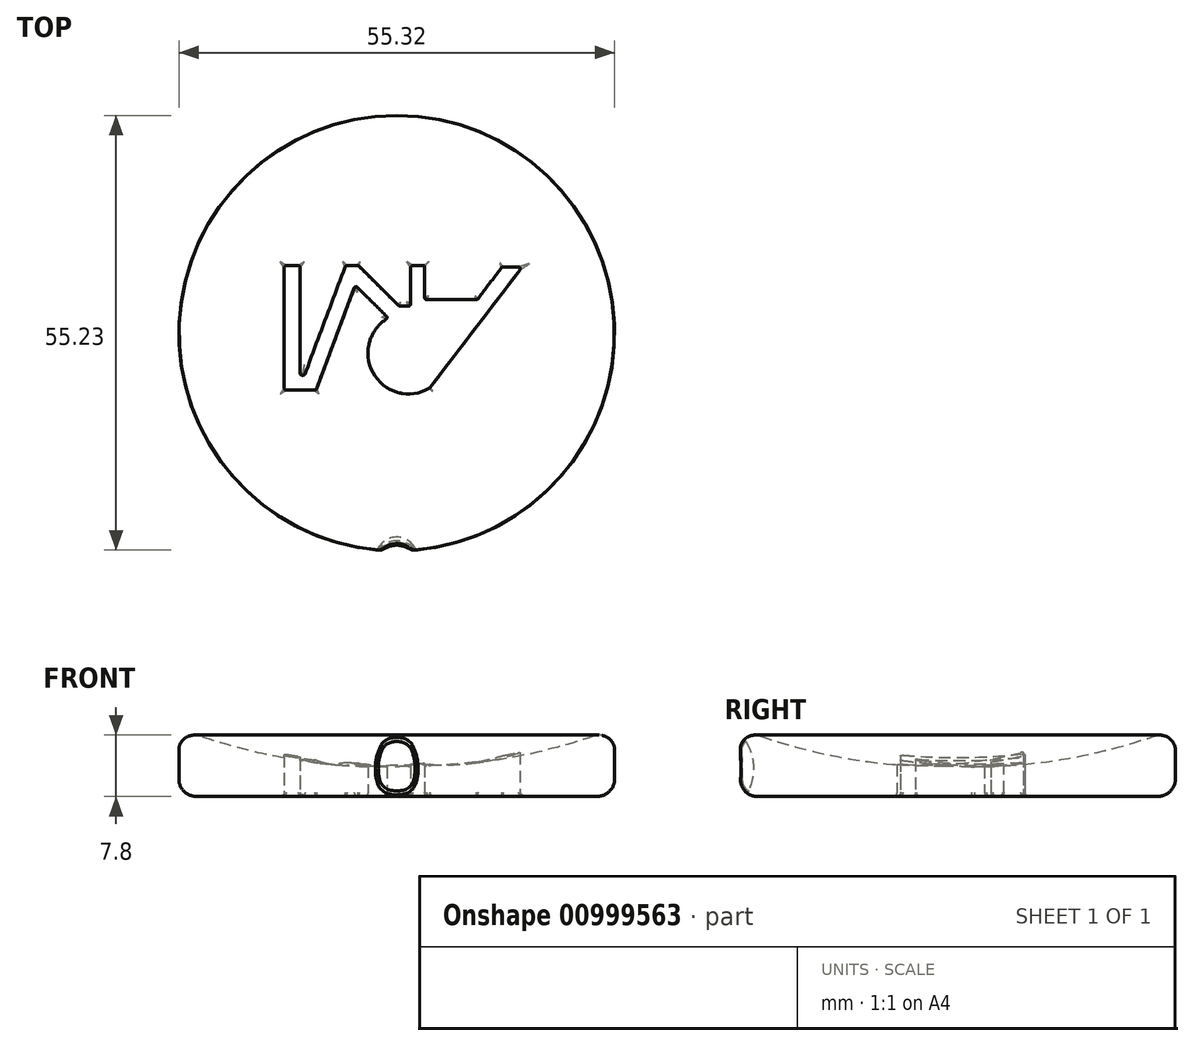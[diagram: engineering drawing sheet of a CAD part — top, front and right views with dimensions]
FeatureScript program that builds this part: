
annotation { "Feature Type Name" : "Feature", "Feature Type Description" : "" }
export const myFeature = defineFeature(function(context is Context, id is Id, definition is map)
    precondition{}
    {
        {
            var Q0;
            Q0=qCreatedBy(makeId("Front.planeOp"),FACE);
            var sketch = newSketch(context, id + "F0", { "sketchPlane" : qUnion([Q0])});
            skLineSegment(sketch, "E0", {"start": v(0, 0) * mm, "end": v(-25.4, 0) * mm});
            skLineSegment(sketch, "E1", {"start": v(0, 0) * mm, "end": v(0, 3.81) * mm});
            skLineSegment(sketch, "E2", {"start": v(-25.16, 7.73) * mm, "end": v(-27.66, 6.26) * mm});
            skLineSegment(sketch, "E3", {"start": v(-25.4, 0) * mm, "end": v(-27.66, 1.82) * mm});
            skLineSegment(sketch, "E4", {"start": v(-27.66, 6.26) * mm, "end": v(-27.66, 1.82) * mm});
            skArc(sketch, "E5", {"start": v(-25.16, 7.73) * mm, "mid": v(-26.72, 7.53) * mm, "end": v(-27.66, 6.26) * mm});
            skArc(sketch, "E6", {"start": v(-25.4, 0) * mm, "mid": v(-26.85, 0.51) * mm, "end": v(-27.66, 1.82) * mm});
            skArc(sketch, "E7", {"start": v(-25.16, 7.73) * mm, "mid": v(-12.76, 4.64) * mm, "end": v(0, 3.81) * mm});
            skSolve(sketch);
        }
        {
            var Q0;
            Q0=qSketchRegion(id+"F0",true);
            var Q1;
            Q1=sQuery(id+"F0.wireOp",EDGE,"E1");
            revolve(context, id + "F1", {"surfaceOperationType" : NewSurfaceOperationType.NEW, "entities" : qUnion([Q0]), "axis" : qUnion([Q1]), "revolveType" : RevolveType.FULL});
        }
        {
            var Q0;
            Q0=makeQuery(id+"F1.opRevolve","SWEPT_FACE",FACE,{"disambiguationData":[OSD([sQuery(id+"F0.wireOp",EDGE,"E0")])]});
            var sketch = newSketch(context, id + "F2", { "sketchPlane" : qUnion([Q0])});
            skLineSegment(sketch, "E8", {"start": v(15.95, -8.4) * mm, "end": v(13.39, -8.4) * mm});
            skLineSegment(sketch, "E9", {"start": v(13.39, -8.4) * mm, "end": v(10.22, -4.26) * mm});
            skLineSegment(sketch, "E10", {"start": v(-5.26, -6.09) * mm, "end": v(-1.09, -1.93) * mm});
            skLineSegment(sketch, "E11", {"start": v(1.78, -8.57) * mm, "end": v(1.78, -3.45) * mm});
            skLineSegment(sketch, "E12", {"start": v(0.27, -3.45) * mm, "end": v(1.78, -3.45) * mm});
            skLineSegment(sketch, "E13", {"start": v(-5.26, -6.09) * mm, "end": v(-10.26, 7.25) * mm});
            skLineSegment(sketch, "E14", {"start": v(-10.26, 7.25) * mm, "end": v(-14.3, 7.25) * mm});
            skLineSegment(sketch, "E15", {"start": v(0.27, -3.45) * mm, "end": v(-4.87, -8.57) * mm});
            skLineSegment(sketch, "E16", {"start": v(-4.87, -8.57) * mm, "end": v(-6.5, -8.57) * mm});
            skLineSegment(sketch, "E17", {"start": v(-14.3, 7.25) * mm, "end": v(-14.3, -8.57) * mm});
            skLineSegment(sketch, "E18", {"start": v(-14.3, -8.57) * mm, "end": v(-12.26, -8.57) * mm});
            skLineSegment(sketch, "E19", {"start": v(-12.26, -8.57) * mm, "end": v(-12.26, 5.36) * mm});
            skLineSegment(sketch, "E20", {"start": v(-6.5, -8.57) * mm, "end": v(-11.72, 5.36) * mm});
            skLineSegment(sketch, "E21", {"start": v(-11.72, 5.36) * mm, "end": v(-12.26, 5.36) * mm});
            skLineSegment(sketch, "E22", {"start": v(3.56, -4.26) * mm, "end": v(3.56, -8.57) * mm});
            skLineSegment(sketch, "E23", {"start": v(1.78, -8.57) * mm, "end": v(3.56, -8.57) * mm});
            skLineSegment(sketch, "E24", {"start": v(3.56, -4.26) * mm, "end": v(10.22, -4.26) * mm});
            skLineSegment(sketch, "E25", {"start": v(15.95, -8.4) * mm, "end": v(4.2, 6.98) * mm});
            skArc(sketch, "E26", {"start": v(4.2, 6.98) * mm, "mid": v(-2.93, 5.18) * mm, "end": v(-1.09, -1.93) * mm});
            skLineSegment(sketch, "E27", {"start": v(-25.27, 2.54) * mm, "end": v(1.52, 2.54) * mm, "construction": true});
            skLineSegment(sketch, "E28", {"start": v(1.52, 25.35) * mm, "end": v(1.52, 2.54) * mm, "construction": true});
            skSolve(sketch);
        }
        {
            var Q0;
            Q0=qSketchRegion(id+"F2",true);
            extrude(context, id + "F3", {"entities" : qUnion([Q0]), "operationType" : NewBodyOperationType.REMOVE, "oppositeDirection" : true, "depth" : 25.4 * mm, "offsetDistance" : 25.4 * mm});
        }
        {
            var Q0;
            Q0=makeQuery(id+"F1.opRevolve","SWEPT_FACE",FACE,{"disambiguationData":[OSD([sQuery(id+"F0.wireOp",EDGE,"QW37AbBs-Tnbc-QzFo-oYAL-jdrFPINPmVJO")])]});
            var Q1;
            Q1=makeQuery(id+"F1.opRevolve","SWEPT_FACE",FACE,{"disambiguationData":[OSD([sQuery(id+"F0.wireOp",EDGE,"E0")])]});
            fillet(context, id + "F4", {"entities" : qUnion([Q0, Q1]), "radius" : 0.5 * mm, "tangentPropagation" : true, "allowEdgeOverflow" : false});
        }
        {
            var Q0;
            Q0=makeQuery(id+"F3.boolean.opBoolean","COPY",EDGE,{"derivedFrom":makeQuery(id+"F3.opExtrude","SWEPT_EDGE",EDGE,{"disambiguationData":[OSD([sQuery(id+"F2.wireOp",EDGE,"E16"),sQuery(id+"F2.wireOp",EDGE,"E20")])]})});
            var Q1;
            Q1=makeQuery(id+"F3.boolean.opBoolean","COPY",EDGE,{"derivedFrom":makeQuery(id+"F3.opExtrude","SWEPT_EDGE",EDGE,{"disambiguationData":[OSD([sQuery(id+"F2.wireOp",EDGE,"E15"),sQuery(id+"F2.wireOp",EDGE,"E16")])]})});
            var Q2;
            Q2=makeQuery(id+"F3.boolean.opBoolean","COPY",EDGE,{"derivedFrom":makeQuery(id+"F3.opExtrude","SWEPT_EDGE",EDGE,{"disambiguationData":[OSD([sQuery(id+"F2.wireOp",EDGE,"E20"),sQuery(id+"F2.wireOp",EDGE,"E21")])]})});
            var Q3;
            Q3=makeQuery(id+"F3.boolean.opBoolean","COPY",EDGE,{"derivedFrom":makeQuery(id+"F3.opExtrude","SWEPT_EDGE",EDGE,{"disambiguationData":[OSD([sQuery(id+"F2.wireOp",EDGE,"E19"),sQuery(id+"F2.wireOp",EDGE,"E21")])]})});
            var Q4;
            Q4=makeQuery(id+"F3.boolean.opBoolean","COPY",EDGE,{"derivedFrom":makeQuery(id+"F3.opExtrude","SWEPT_EDGE",EDGE,{"disambiguationData":[OSD([sQuery(id+"F2.wireOp",EDGE,"E13"),sQuery(id+"F2.wireOp",EDGE,"E14")])]})});
            var Q5;
            Q5=makeQuery(id+"F3.boolean.opBoolean","COPY",EDGE,{"derivedFrom":makeQuery(id+"F3.opExtrude","SWEPT_EDGE",EDGE,{"disambiguationData":[OSD([sQuery(id+"F2.wireOp",EDGE,"E10"),sQuery(id+"F2.wireOp",EDGE,"E13")])]})});
            var Q6;
            Q6=makeQuery(id+"F3.boolean.opBoolean","COPY",EDGE,{"derivedFrom":makeQuery(id+"F3.opExtrude","SWEPT_EDGE",EDGE,{"disambiguationData":[OSD([sQuery(id+"F2.wireOp",EDGE,"E14"),sQuery(id+"F2.wireOp",EDGE,"E17")])]})});
            var Q7;
            Q7=makeQuery(id+"F3.boolean.opBoolean","COPY",EDGE,{"derivedFrom":makeQuery(id+"F3.opExtrude","SWEPT_EDGE",EDGE,{"disambiguationData":[OSD([sQuery(id+"F2.wireOp",EDGE,"E17"),sQuery(id+"F2.wireOp",EDGE,"E18")])]})});
            var Q8;
            Q8=makeQuery(id+"F3.boolean.opBoolean","COPY",EDGE,{"derivedFrom":makeQuery(id+"F3.opExtrude","SWEPT_EDGE",EDGE,{"disambiguationData":[OSD([sQuery(id+"F2.wireOp",EDGE,"E18"),sQuery(id+"F2.wireOp",EDGE,"E19")])]})});
            var Q9;
            Q9=makeQuery(id+"F3.boolean.opBoolean","COPY",EDGE,{"derivedFrom":makeQuery(id+"F3.opExtrude","SWEPT_EDGE",EDGE,{"disambiguationData":[OSD([sQuery(id+"F2.wireOp",EDGE,"E10"),sQuery(id+"F2.wireOp",EDGE,"E26")])]})});
            var Q10;
            Q10=makeQuery(id+"F3.boolean.opBoolean","COPY",EDGE,{"derivedFrom":makeQuery(id+"F3.opExtrude","SWEPT_EDGE",EDGE,{"disambiguationData":[OSD([sQuery(id+"F2.wireOp",EDGE,"E12"),sQuery(id+"F2.wireOp",EDGE,"E15")])]})});
            var Q11;
            Q11=makeQuery(id+"F3.boolean.opBoolean","COPY",EDGE,{"derivedFrom":makeQuery(id+"F3.opExtrude","SWEPT_EDGE",EDGE,{"disambiguationData":[OSD([sQuery(id+"F2.wireOp",EDGE,"E11"),sQuery(id+"F2.wireOp",EDGE,"E12")])]})});
            var Q12;
            Q12=makeQuery(id+"F3.boolean.opBoolean","COPY",EDGE,{"derivedFrom":makeQuery(id+"F3.opExtrude","SWEPT_EDGE",EDGE,{"disambiguationData":[OSD([sQuery(id+"F2.wireOp",EDGE,"E25"),sQuery(id+"F2.wireOp",EDGE,"E26")])]})});
            var Q13;
            Q13=makeQuery(id+"F3.boolean.opBoolean","COPY",EDGE,{"derivedFrom":makeQuery(id+"F3.opExtrude","SWEPT_EDGE",EDGE,{"disambiguationData":[OSD([sQuery(id+"F2.wireOp",EDGE,"E11"),sQuery(id+"F2.wireOp",EDGE,"E23")])]})});
            var Q14;
            {var subQ0=makeQuery(id+"F3.opExtrude","SWEPT_FACE",FACE,{"disambiguationData":[OSD([sQuery(id+"F2.wireOp",EDGE,"E22")])]});Q14=makeQuery(id+"F4.opFillet","BLEND_EDGE",EDGE,{"blendedFrom":[makeQuery(id+"F3.boolean.opBoolean","INTERSECT",EDGE,{"derivedFrom":[makeQuery(id+"F1.opRevolve","SWEPT_FACE",FACE,{"disambiguationData":[OSD([sQuery(id+"F0.wireOp",EDGE,"QW37AbBs-Tnbc-QzFo-oYAL-jdrFPINPmVJO")])]}),subQ0]}),makeQuery(id+"F3.boolean.opBoolean","COPY",FACE,{"derivedFrom":subQ0})],"blendedInto":[makeQuery(id+"F3.boolean.opBoolean","COPY",FACE,{"derivedFrom":subQ0})]});}
            var Q15;
            Q15=makeQuery(id+"F3.boolean.opBoolean","COPY",EDGE,{"derivedFrom":makeQuery(id+"F3.opExtrude","SWEPT_EDGE",EDGE,{"disambiguationData":[OSD([sQuery(id+"F2.wireOp",EDGE,"E22"),sQuery(id+"F2.wireOp",EDGE,"E24")])]})});
            var Q16;
            Q16=makeQuery(id+"F3.boolean.opBoolean","COPY",EDGE,{"derivedFrom":makeQuery(id+"F3.opExtrude","SWEPT_EDGE",EDGE,{"disambiguationData":[OSD([sQuery(id+"F2.wireOp",EDGE,"E9"),sQuery(id+"F2.wireOp",EDGE,"E24")])]})});
            var Q17;
            Q17=makeQuery(id+"F3.boolean.opBoolean","COPY",EDGE,{"derivedFrom":makeQuery(id+"F3.opExtrude","SWEPT_EDGE",EDGE,{"disambiguationData":[OSD([sQuery(id+"F2.wireOp",EDGE,"E8"),sQuery(id+"F2.wireOp",EDGE,"E9")])]})});
            var Q18;
            Q18=makeQuery(id+"F3.boolean.opBoolean","COPY",EDGE,{"derivedFrom":makeQuery(id+"F3.opExtrude","SWEPT_EDGE",EDGE,{"disambiguationData":[OSD([sQuery(id+"F2.wireOp",EDGE,"E8"),sQuery(id+"F2.wireOp",EDGE,"E25")])]})});
            fillet(context, id + "F5", {"entities" : qUnion([Q0, Q1, Q2, Q3, Q4, Q5, Q6, Q7, Q8, Q9, Q10, Q11, Q12, Q13, Q14, Q15, Q16, Q17, Q18]), "radius" : 0.25 * mm, "tangentPropagation" : true, "allowEdgeOverflow" : false});
        }
        {
            var Q0;
            Q0=makeQuery(id+"F1.opRevolve","SWEPT_EDGE",EDGE,{"disambiguationData":[OSD([sQuery(id+"F0.wireOp",EDGE,"E2"),sQuery(id+"F0.wireOp",EDGE,"E4"),sQuery(id+"F0.wireOp",EDGE,"E5")])]});
            var Q1;
            Q1=makeQuery(id+"F1.opRevolve","SWEPT_EDGE",EDGE,{"disambiguationData":[OSD([sQuery(id+"F0.wireOp",EDGE,"E3"),sQuery(id+"F0.wireOp",EDGE,"E4"),sQuery(id+"F0.wireOp",EDGE,"E6")])]});
            fillet(context, id + "F6", {"entities" : qUnion([Q0, Q1]), "radius" : 1.27 * mm, "tangentPropagation" : true, "allowEdgeOverflow" : false});
        }
        {
            var Q0;
            Q0=qCreatedBy(makeId("Right.planeOp"),FACE);
            var sketch = newSketch(context, id + "F7", { "sketchPlane" : qUnion([Q0])});
            skLineSegment(sketch, "E29", {"start": v(-28.57, 0) * mm, "end": v(-28.57, 7.13) * mm});
            skLineSegment(sketch, "E30", {"start": v(-28.57, 7.13) * mm, "end": v(-28.57, 7.99) * mm});
            skPoint(sketch, "E31.endSnap0", {"position": v(-28.57, 7.56) * mm});
            skLineSegment(sketch, "E32", {"start": v(-28.57, 0) * mm, "end": v(-28.57, -0.86) * mm});
            skLineSegment(sketch, "E33", {"start": v(-28.57, -0.86) * mm, "end": v(-28.57, -1.71) * mm});
            skLineSegment(sketch, "E34", {"start": v(-28.57, 7.99) * mm, "end": v(-28.57, 8.84) * mm});
            skArc(sketch, "E35", {"start": v(-28.57, -1.71) * mm, "mid": v(-25.91, 3.56) * mm, "end": v(-28.57, 8.84) * mm});
            skSolve(sketch);
        }
        {
            var Q0;
            Q0=makeQuery(id+"F7.imprint","IMPRINT",FACE,{"disambiguationData":[TD([[makeQuery(id+"F7.imprint","IMPRINT",EDGE,{"derivedFrom":sQuery(id+"F7.wireOp",EDGE,"E29")}),-1.0]])]});
            var Q1;
            Q1=sQuery(id+"F7.wireOp",EDGE,"E29");
            revolve(context, id + "F8", {"operationType" : NewBodyOperationType.REMOVE, "surfaceOperationType" : NewSurfaceOperationType.NEW, "entities" : qUnion([Q0]), "axis" : qUnion([Q1]), "revolveType" : RevolveType.FULL, "oppositeDirection" : true});
        }
        {
            var Q0;
            Q0=makeQuery(id+"F1.opRevolve","SWEPT_EDGE",EDGE,{"disambiguationData":[OSD([sQuery(id+"F0.wireOp",EDGE,"E2"),sQuery(id+"F0.wireOp",EDGE,"E5"),sQuery(id+"F0.wireOp",EDGE,"E7")])]});
            fillet(context, id + "F9", {"entities" : qUnion([Q0]), "radius" : 1.98 * mm, "tangentPropagation" : true, "allowEdgeOverflow" : false});
        }
        {
            var Q0;
            Q0=makeQuery(id+"F66RFeuWNEC0Q9P_1.14.F8.boolean.opBoolean","COPY",FACE,{"derivedFrom":makeQuery(id+"F66RFeuWNEC0Q9P_1.14.F8.opRevolve","SWEPT_FACE",FACE,{"disambiguationData":[OSD([sQuery(id+"F7.wireOp",EDGE,"E35")])]})});
            var Q1;
            Q1=makeQuery(id+"F66RFeuWNEC0Q9P_1.13.F8.boolean.opBoolean","COPY",FACE,{"derivedFrom":makeQuery(id+"F66RFeuWNEC0Q9P_1.13.F8.opRevolve","SWEPT_FACE",FACE,{"disambiguationData":[OSD([sQuery(id+"F7.wireOp",EDGE,"E35")])]})});
            var Q2;
            Q2=makeQuery(id+"F66RFeuWNEC0Q9P_1.12.F8.boolean.opBoolean","COPY",FACE,{"derivedFrom":makeQuery(id+"F66RFeuWNEC0Q9P_1.12.F8.opRevolve","SWEPT_FACE",FACE,{"disambiguationData":[OSD([sQuery(id+"F7.wireOp",EDGE,"E35")])]})});
            var Q3;
            Q3=makeQuery(id+"F66RFeuWNEC0Q9P_1.11.F8.boolean.opBoolean","COPY",FACE,{"derivedFrom":makeQuery(id+"F66RFeuWNEC0Q9P_1.11.F8.opRevolve","SWEPT_FACE",FACE,{"disambiguationData":[OSD([sQuery(id+"F7.wireOp",EDGE,"E35")])]})});
            var Q4;
            Q4=makeQuery(id+"F66RFeuWNEC0Q9P_1.10.F8.boolean.opBoolean","COPY",FACE,{"derivedFrom":makeQuery(id+"F66RFeuWNEC0Q9P_1.10.F8.opRevolve","SWEPT_FACE",FACE,{"disambiguationData":[OSD([sQuery(id+"F7.wireOp",EDGE,"E35")])]})});
            var Q5;
            Q5=makeQuery(id+"F66RFeuWNEC0Q9P_1.9.F8.boolean.opBoolean","COPY",FACE,{"derivedFrom":makeQuery(id+"F66RFeuWNEC0Q9P_1.9.F8.opRevolve","SWEPT_FACE",FACE,{"disambiguationData":[OSD([sQuery(id+"F7.wireOp",EDGE,"E35")])]})});
            var Q6;
            Q6=makeQuery(id+"F66RFeuWNEC0Q9P_1.8.F8.boolean.opBoolean","COPY",FACE,{"derivedFrom":makeQuery(id+"F66RFeuWNEC0Q9P_1.8.F8.opRevolve","SWEPT_FACE",FACE,{"disambiguationData":[OSD([sQuery(id+"F7.wireOp",EDGE,"E35")])]})});
            var Q7;
            Q7=makeQuery(id+"F66RFeuWNEC0Q9P_1.7.F8.boolean.opBoolean","COPY",FACE,{"derivedFrom":makeQuery(id+"F66RFeuWNEC0Q9P_1.7.F8.opRevolve","SWEPT_FACE",FACE,{"disambiguationData":[OSD([sQuery(id+"F7.wireOp",EDGE,"E35")])]})});
            var Q8;
            Q8=makeQuery(id+"F66RFeuWNEC0Q9P_1.6.F8.boolean.opBoolean","COPY",FACE,{"derivedFrom":makeQuery(id+"F66RFeuWNEC0Q9P_1.6.F8.opRevolve","SWEPT_FACE",FACE,{"disambiguationData":[OSD([sQuery(id+"F7.wireOp",EDGE,"E35")])]})});
            var Q9;
            Q9=makeQuery(id+"F66RFeuWNEC0Q9P_1.5.F8.boolean.opBoolean","COPY",FACE,{"derivedFrom":makeQuery(id+"F66RFeuWNEC0Q9P_1.5.F8.opRevolve","SWEPT_FACE",FACE,{"disambiguationData":[OSD([sQuery(id+"F7.wireOp",EDGE,"E35")])]})});
            var Q10;
            Q10=makeQuery(id+"F66RFeuWNEC0Q9P_1.4.F8.boolean.opBoolean","COPY",FACE,{"derivedFrom":makeQuery(id+"F66RFeuWNEC0Q9P_1.4.F8.opRevolve","SWEPT_FACE",FACE,{"disambiguationData":[OSD([sQuery(id+"F7.wireOp",EDGE,"E35")])]})});
            var Q11;
            Q11=makeQuery(id+"F66RFeuWNEC0Q9P_1.3.F8.boolean.opBoolean","COPY",FACE,{"derivedFrom":makeQuery(id+"F66RFeuWNEC0Q9P_1.3.F8.opRevolve","SWEPT_FACE",FACE,{"disambiguationData":[OSD([sQuery(id+"F7.wireOp",EDGE,"E35")])]})});
            var Q12;
            Q12=makeQuery(id+"F66RFeuWNEC0Q9P_1.2.F8.boolean.opBoolean","COPY",FACE,{"derivedFrom":makeQuery(id+"F66RFeuWNEC0Q9P_1.2.F8.opRevolve","SWEPT_FACE",FACE,{"disambiguationData":[OSD([sQuery(id+"F7.wireOp",EDGE,"E35")])]})});
            var Q13;
            Q13=makeQuery(id+"F66RFeuWNEC0Q9P_1.1.F8.boolean.opBoolean","COPY",FACE,{"derivedFrom":makeQuery(id+"F66RFeuWNEC0Q9P_1.1.F8.opRevolve","SWEPT_FACE",FACE,{"disambiguationData":[OSD([sQuery(id+"F7.wireOp",EDGE,"E35")])]})});
            var Q14;
            Q14=makeQuery(id+"F8.boolean.opBoolean","COPY",FACE,{"derivedFrom":makeQuery(id+"F8.opRevolve","SWEPT_FACE",FACE,{"disambiguationData":[OSD([sQuery(id+"F7.wireOp",EDGE,"E35")])]})});
            fillet(context, id + "F10", {"entities" : qUnion([Q0, Q1, Q2, Q3, Q4, Q5, Q6, Q7, Q8, Q9, Q10, Q11, Q12, Q13, Q14]), "radius" : 0.38 * mm, "tangentPropagation" : true, "allowEdgeOverflow" : false});
        }
    });
